# Revit family: SANINDUSA_142022004_Winner_WinnerWDrimFlushCloseCoupledToilet350x630x400_V0
name_source: partatom
category: Plumbing Fixtures
units: mm (PartAtom-declared; Revit-internal decimal feet)

## family parameters
Cut with Voids When Loaded = No
Host = Face
Part Type = Normal
Room Calculation Point = No
Round Connector Dimension = Use Diameter
Shared = No

## types (1)
- SANINDUSA_142022004_Winner_WinnerWDrimFlushCloseCoupledToilet350x630x400_V0
    AssetType = Fixed
    CodePerformance = EN 997:2012+A1:2015    CL 1 - 6 A
    Color = white
    Constituents = Compatible toilet seats (not included): 24231 - Winner toilet seat with easyclip system: 142111LM - Winner bottom water supply cistern with dual flush mechanism; 142113LM - Winner side water supply cistern with dual flush mechanism: 24 - fixing kit (included): D90 "S" trap pan connector (included).
    Default Elevation = 1219 mm
    Description = Soil appliance for the disposal of excrement.
    DrainSize = 100 mm  [stored 0.328084 ft]
    Element Type = TOILETPAN: Soil appliance for the disposal of excrement.
    Features = "Domestic and commercial use. Versatile timeless design. Seats easy to clean and slow close option. "
    Finish = gloss
    InletDiameter = 0 mm  [stored 0 ft]
    Installation Instructions = https://www.tec.sanindusa.pt
    Manufacturer = Sanindusa
    ManufacturerName = Sanindusa
    ManufacturerURL = www.tec.sanindusa.pt
    Material = vitreous china
    Model = 142022004
    ModelNumber = 142022004
    ModelReference = Winner
    Name = Winner W/D rimflush close coupled toilet
    NominalHeight = 400 mm  [stored 1.31234 ft]
    NominalLength = 350 mm  [stored 1.14829 ft]
    NominalWidth = 630 mm  [stored 2.06693 ft]
    PanColor = white
    PanMaterial = vitreous china
    PanMounting = pedestal
    Pre-defined type (IFC) = TOILETPAN
    ProductInformation = https://www.tec.sanindusa.pt
    ProductionYear = 2020
    Size = 350x630x400
    ToiletPanType = washdown
    ToiletType = LooseCoupled
    Type (IFC) = IfcSanitaryTerminalType
    URL = www.tec.sanindusa.pt
    Version = 1
    WarrantyDescription = https://www.tec.sanindusa.pt
    WarrantyDurationParts = 5
    WarrantyDurationUnit = year
    Waste Connection = Yes
    Weight = 23.00 kg

note: [stored X ft] marks values corroborated as IEEE doubles in the binary element streams (Revit-internal decimal feet)

## geometry (parser evidence)
native form markers: Sweep x8
no freeform markers — native parametric forms only
